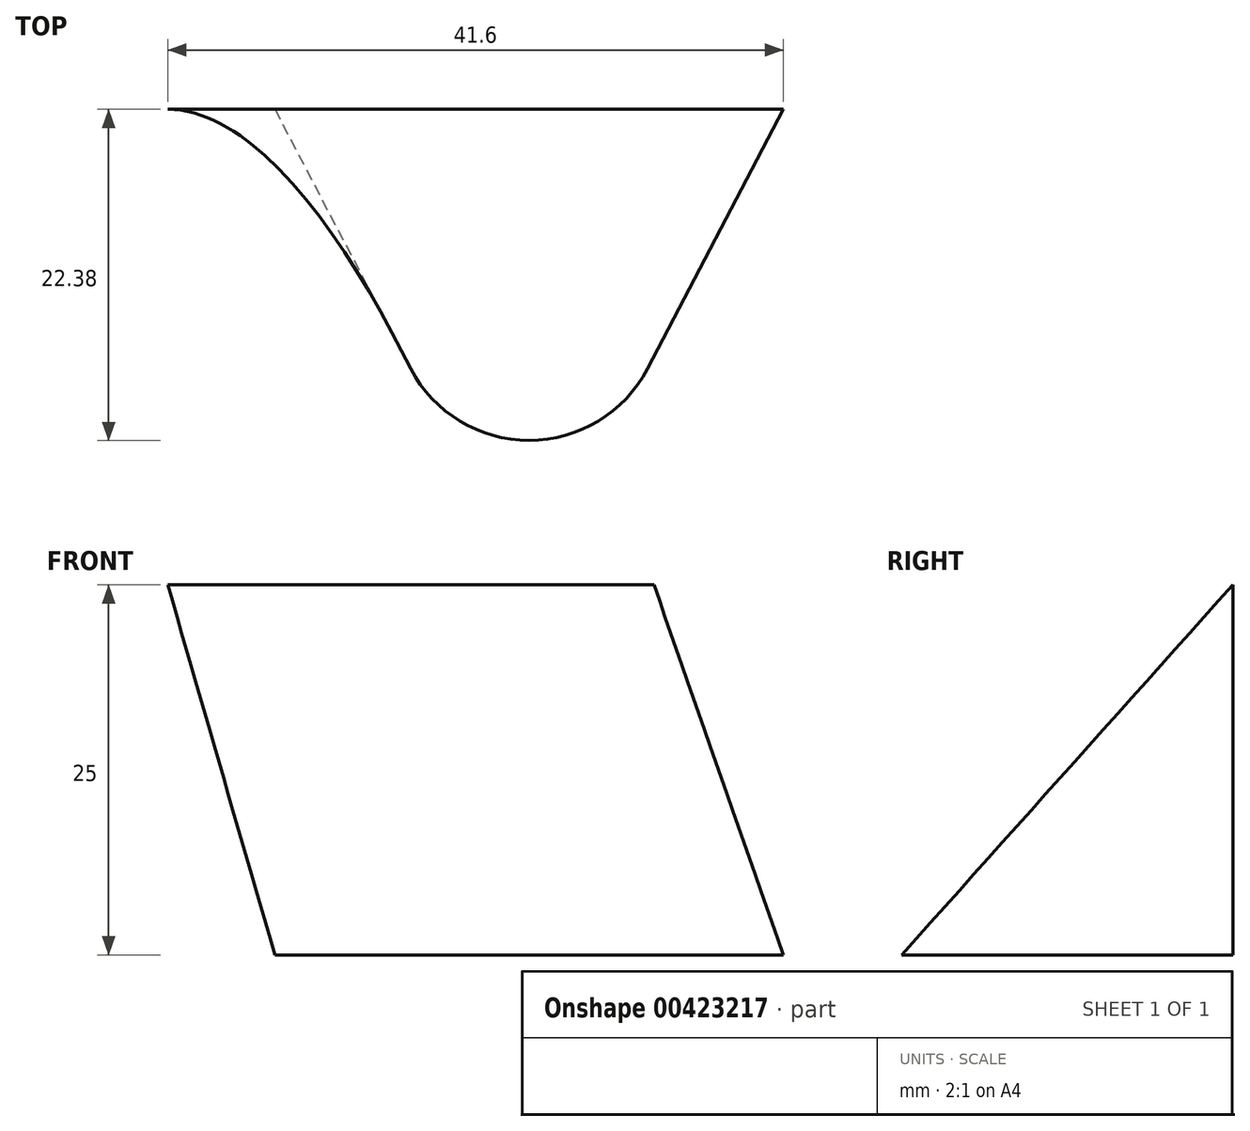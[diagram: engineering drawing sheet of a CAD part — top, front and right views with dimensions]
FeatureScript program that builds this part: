
annotation { "Feature Type Name" : "Feature", "Feature Type Description" : "" }
export const myFeature = defineFeature(function(context is Context, id is Id, definition is map)
    precondition{}
    {
        {
            var Q0;
            Q0=qCreatedBy(makeId("Top.planeOp"),FACE);
            var sketch = newSketch(context, id + "F0", { "sketchPlane" : qUnion([Q0])});
            skLineSegment(sketch, "E0.bottom", {"start": v(-54.85, 0) * mm, "end": v(54.85, 0) * mm});
            skLineSegment(sketch, "E0.top", {"start": v(-54.85, -63.98) * mm, "end": v(54.85, -63.98) * mm});
            skLineSegment(sketch, "E0.left", {"start": v(54.85, 0) * mm, "end": v(54.85, -63.98) * mm});
            skLineSegment(sketch, "E0.right", {"start": v(-54.85, 0) * mm, "end": v(-54.85, -63.98) * mm});
            skCircle(sketch, "E1", {"center": v(-40, 40) * mm, "radius": 4 * mm});
            skCircle(sketch, "E2", {"center": v(40, 40) * mm, "radius": 4 * mm});
            skCircle(sketch, "E3", {"center": v(0, 40) * mm, "radius": 11.5 * mm});
            skLineSegment(sketch, "E4.bottom", {"start": v(-70, 70) * mm, "end": v(70, 70) * mm});
            skLineSegment(sketch, "E4.top", {"start": v(-70, -110) * mm, "end": v(70, -110) * mm});
            skLineSegment(sketch, "E4.left", {"start": v(-90, 50) * mm, "end": v(-90, -90) * mm});
            skLineSegment(sketch, "E4.right", {"start": v(90, 50) * mm, "end": v(90, -90) * mm});
            skPoint(sketch, "E5.visualSharp", {"position": v(-90, 70) * mm});
            skArc(sketch, "E5.filletArc", {"start": v(-70, 70) * mm, "mid": v(-84.14, 64.14) * mm, "end": v(-90, 50) * mm});
            skPoint(sketch, "E6.visualSharp", {"position": v(90, 70) * mm});
            skArc(sketch, "E6.filletArc", {"start": v(90, 50) * mm, "mid": v(84.14, 64.14) * mm, "end": v(70, 70) * mm});
            skPoint(sketch, "E7.visualSharp", {"position": v(90, -110) * mm});
            skArc(sketch, "E7.filletArc", {"start": v(70, -110) * mm, "mid": v(84.14, -104.14) * mm, "end": v(90, -90) * mm});
            skPoint(sketch, "E8.visualSharp", {"position": v(-90, -110) * mm});
            skArc(sketch, "E8.filletArc", {"start": v(-90, -90) * mm, "mid": v(-84.14, -104.14) * mm, "end": v(-70, -110) * mm});
            skPoint(sketch, "E9", {"position": v(-90, -32) * mm});
            skPoint(sketch, "E9.positionSnap0", {"position": v(-54.85, -32) * mm});
            skPoint(sketch, "E10", {"position": v(54.85, -32) * mm});
            skPoint(sketch, "E11", {"position": v(90, -32) * mm});
            skCircle(sketch, "E12", {"center": v(-73.09, -32) * mm, "radius": 3 * mm});
            skCircle(sketch, "E13", {"center": v(72.43, -32) * mm, "radius": 3 * mm});
            skPoint(sketch, "E14", {"position": v(0, 70) * mm});
            skPoint(sketch, "E15", {"position": v(0, -110) * mm});
            skLineSegment(sketch, "E16.bottom", {"start": v(16, 24) * mm, "end": v(-16, 24) * mm, "construction": true});
            skLineSegment(sketch, "E16.top", {"start": v(16, 56) * mm, "end": v(-16, 56) * mm, "construction": true});
            skLineSegment(sketch, "E16.left", {"start": v(16, 24) * mm, "end": v(16, 56) * mm, "construction": true});
            skLineSegment(sketch, "E16.right", {"start": v(-16, 24) * mm, "end": v(-16, 56) * mm, "construction": true});
            skCircle(sketch, "E17", {"center": v(-16, 56) * mm, "radius": 2 * mm});
            skCircle(sketch, "E18", {"center": v(16, 56) * mm, "radius": 2 * mm});
            skCircle(sketch, "E19", {"center": v(16, 24) * mm, "radius": 2 * mm});
            skCircle(sketch, "E20", {"center": v(-16, 24) * mm, "radius": 2 * mm});
            skCircle(sketch, "E21", {"center": v(-40, 40) * mm, "radius": 7 * mm});
            skCircle(sketch, "E22", {"center": v(40, 40) * mm, "radius": 7 * mm});
            skCircle(sketch, "E23", {"center": v(0, 40) * mm, "radius": 5 * mm});
            skLineSegment(sketch, "E24.0", {"start": v(-46.85, -3) * mm, "end": v(46.85, -3) * mm});
            skLineSegment(sketch, "E24.1", {"start": v(-51.85, -8) * mm, "end": v(-51.85, -55.98) * mm});
            skLineSegment(sketch, "E24.2", {"start": v(-46.85, -60.98) * mm, "end": v(46.85, -60.98) * mm});
            skLineSegment(sketch, "E24.3", {"start": v(51.85, -8) * mm, "end": v(51.85, -55.98) * mm});
            skPoint(sketch, "E25.visualSharp", {"position": v(-51.85, -3) * mm});
            skArc(sketch, "E25.filletArc", {"start": v(-46.85, -3) * mm, "mid": v(-50.39, -4.46) * mm, "end": v(-51.85, -8) * mm});
            skPoint(sketch, "E26.visualSharp", {"position": v(-51.85, -60.98) * mm});
            skArc(sketch, "E26.filletArc", {"start": v(-51.85, -55.98) * mm, "mid": v(-50.39, -59.52) * mm, "end": v(-46.85, -60.98) * mm});
            skPoint(sketch, "E27.visualSharp", {"position": v(51.85, -3) * mm});
            skArc(sketch, "E27.filletArc", {"start": v(51.85, -8) * mm, "mid": v(50.39, -4.46) * mm, "end": v(46.85, -3) * mm});
            skPoint(sketch, "E28.visualSharp", {"position": v(51.85, -60.98) * mm});
            skArc(sketch, "E28.filletArc", {"start": v(46.85, -60.98) * mm, "mid": v(50.39, -59.52) * mm, "end": v(51.85, -55.98) * mm});
            skPoint(sketch, "E29", {"position": v(0, -32) * mm});
            skPoint(sketch, "E29.positionSnap0", {"position": v(51.85, -32) * mm});
            skCircle(sketch, "E30", {"center": v(0, -32) * mm, "radius": 4 * mm});
            skCircle(sketch, "E31", {"center": v(0, -32) * mm, "radius": 9.03 * mm});
            skLineSegment(sketch, "E32", {"start": v(-46.2, 36.75) * mm, "end": v(-8, -36.18) * mm});
            skLineSegment(sketch, "E33", {"start": v(8, -36.18) * mm, "end": v(46.2, 36.75) * mm});
            skLineSegment(sketch, "E34", {"start": v(-40, 47) * mm, "end": v(40, 47) * mm});
            skSolve(sketch);
        }
        {
            var Q0;
            Q0=qCreatedBy(makeId("Top.planeOp"),FACE);
            var sketch = newSketch(context, id + "F1", { "sketchPlane" : qUnion([Q0])});
            skLineSegment(sketch, "E35.bottom", {"start": v(-36.15, -18.65) * mm, "end": v(35.6, -18.65) * mm});
            skLineSegment(sketch, "E35.top", {"start": v(-36.15, -45.02) * mm, "end": v(35.6, -45.02) * mm});
            skLineSegment(sketch, "E35.left", {"start": v(-36.15, -18.65) * mm, "end": v(-36.15, -45.02) * mm});
            skLineSegment(sketch, "E35.right", {"start": v(35.6, -18.65) * mm, "end": v(35.6, -45.02) * mm});
            skSolve(sketch);
        }
        {
            var Q0;
            Q0 = qSketchRegion(id + "F1", true);
            extrude(context, id + "F2", {"entities" : qUnion([Q0]), "depth" : 25 * mm});
        }
        {
            var Q0;
            Q0=makeQuery(id+"F2.opExtrude","SWEPT_EDGE",EDGE,{"disambiguationData":[OSD([sQuery(id+"F1.wireOp",EDGE,"E35.top"),sQuery(id+"F1.wireOp",EDGE,"E35.left")])]});
            var Q1;
            Q1=makeQuery(id+"F2.opExtrude","SWEPT_EDGE",EDGE,{"disambiguationData":[OSD([sQuery(id+"F1.wireOp",EDGE,"E35.top"),sQuery(id+"F1.wireOp",EDGE,"E35.right")])]});
            var Q2;
            Q2=makeQuery(id+"F2.opExtrude","SWEPT_EDGE",EDGE,{"disambiguationData":[OSD([sQuery(id+"F1.wireOp",EDGE,"E35.bottom"),sQuery(id+"F1.wireOp",EDGE,"E35.right")])]});
            var Q3;
            Q3=makeQuery(id+"F2.opExtrude","SWEPT_EDGE",EDGE,{"disambiguationData":[OSD([sQuery(id+"F1.wireOp",EDGE,"E35.bottom"),sQuery(id+"F1.wireOp",EDGE,"E35.left")])]});
            fillet(context, id + "F3", {"entities" : qUnion([Q0, Q1, Q2, Q3]), "radius" : 5 * mm, "tangentPropagation" : true, "allowEdgeOverflow" : false});
        }
        {
            var Q1;
            Q1=makeQuery(id+"F0.imprint","IMPRINT",FACE,{"disambiguationData":[TD([[makeQuery(id+"F0.imprint","IMPRINT",EDGE,{"derivedFrom":sQuery(id+"F0.wireOp",EDGE,"E24.1")}),1.0]])]});
            var Q2;
            Q2=makeQuery(id+"F2.opExtrude","CAP_FACE",FACE,{"disambiguationData":[OSD([sQuery(id+"F1.wireOp",EDGE,"E35.bottom"),sQuery(id+"F1.wireOp",EDGE,"E35.top"),sQuery(id+"F1.wireOp",EDGE,"E35.left"),sQuery(id+"F1.wireOp",EDGE,"E35.right")])],"isStart":false});
            loft(context, id + "F4", {"operationType" : NewBodyOperationType.REMOVE, "sheetProfilesArray" : [{ "sheetProfileEntities" : qUnion([Q1]) }, { "sheetProfileEntities" : qUnion([Q2]) }]});
        }
    });
